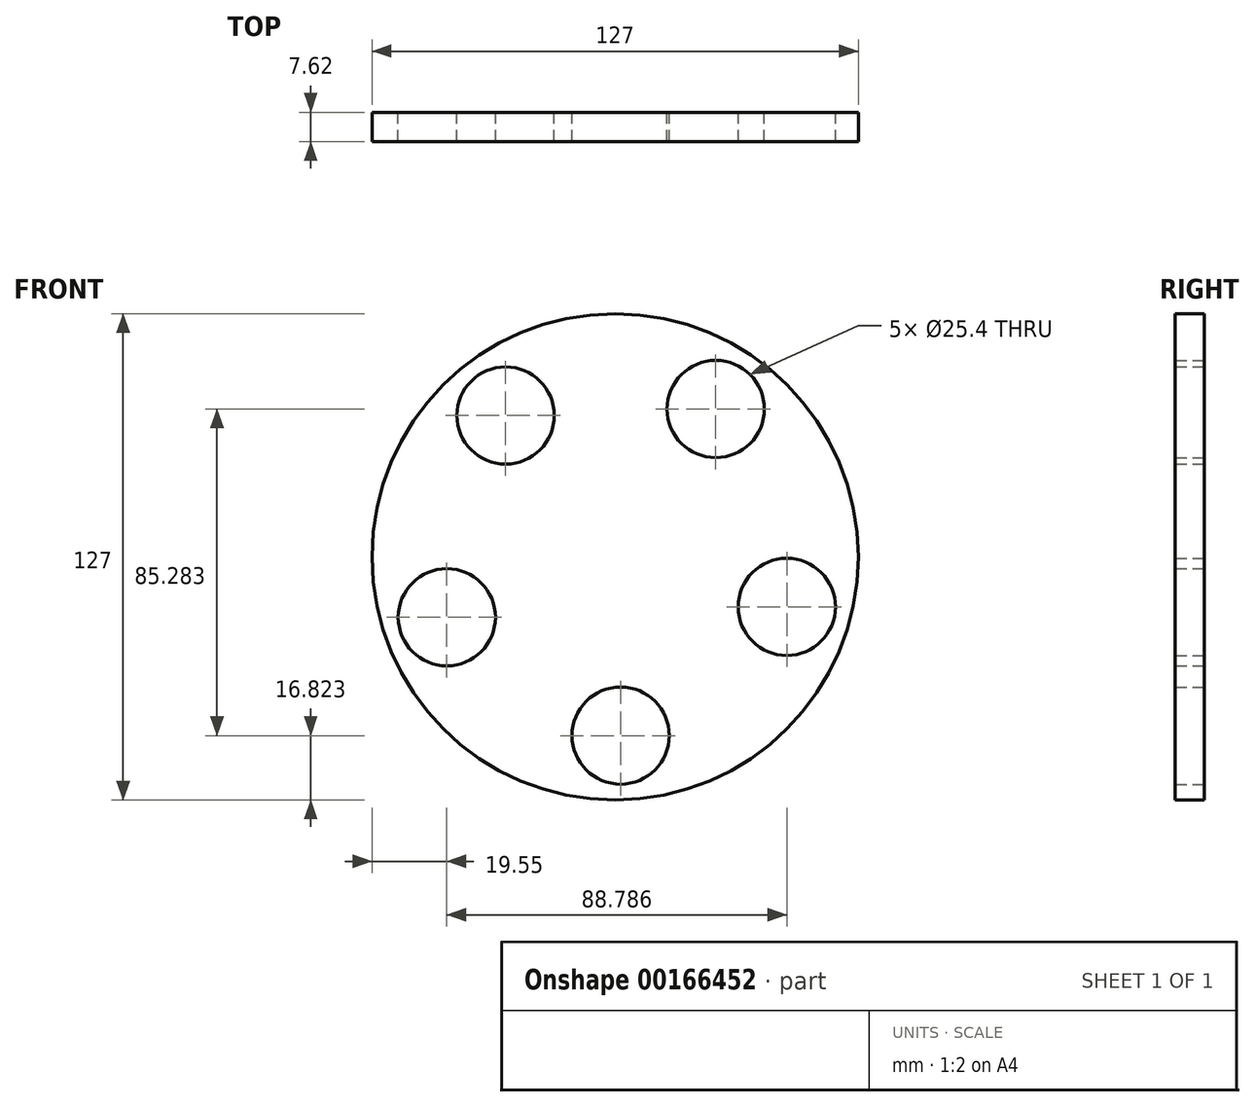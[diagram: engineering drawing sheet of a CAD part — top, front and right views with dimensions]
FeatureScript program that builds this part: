
annotation { "Feature Type Name" : "Feature", "Feature Type Description" : "" }
export const myFeature = defineFeature(function(context is Context, id is Id, definition is map)
    precondition{}
    {
        {
            var Q0;
            Q0=qCreatedBy(makeId("Front.planeOp"),FACE);
            var sketch = newSketch(context, id + "F0", { "sketchPlane" : qUnion([Q0])});
            skCircle(sketch, "E0", {"center": v(0, 0) * mm, "radius": 63.5 * mm});
            skSolve(sketch);
        }
        {
            var Q0;
            Q0=makeQuery(id+"F0.imprint","IMPRINT",FACE,{"disambiguationData":[TD([[makeQuery(id+"F0.imprint","IMPRINT",EDGE,{"derivedFrom":sQuery(id+"F0.wireOp",EDGE,"E0")}),1.0]])]});
            extrude(context, id + "F1", {"entities" : qUnion([Q0]), "depth" : 7.62 * mm});
        }
        {
            var Q0;
            Q0=qCreatedBy(makeId("Front.planeOp"),FACE);
            var sketch = newSketch(context, id + "F2", { "sketchPlane" : qUnion([Q0])});
            skCircle(sketch, "E1", {"center": v(-28.6, 36.92) * mm, "radius": 12.7 * mm});
            skCircle(sketch, "E2.1.0", {"center": v(-43.95, -15.79) * mm, "radius": 12.7 * mm});
            skCircle(sketch, "E2.2.0", {"center": v(1.43, -46.68) * mm, "radius": 12.7 * mm});
            skCircle(sketch, "E2.3.0", {"center": v(44.84, -13.06) * mm, "radius": 12.7 * mm});
            skCircle(sketch, "E2.4.0", {"center": v(26.28, 38.6) * mm, "radius": 12.7 * mm});
            skPoint(sketch, "E2.center", {"position": v(0, 0) * mm});
            skSolve(sketch);
        }
        {
            var Q0;
            Q0 = qSketchRegion(id + "F2", true);
            extrude(context, id + "F3", {"entities" : qUnion([Q0]), "operationType" : NewBodyOperationType.REMOVE, "endBound" : BoundingType.THROUGH_ALL, "depth" : 25.4 * mm});
        }
    });
